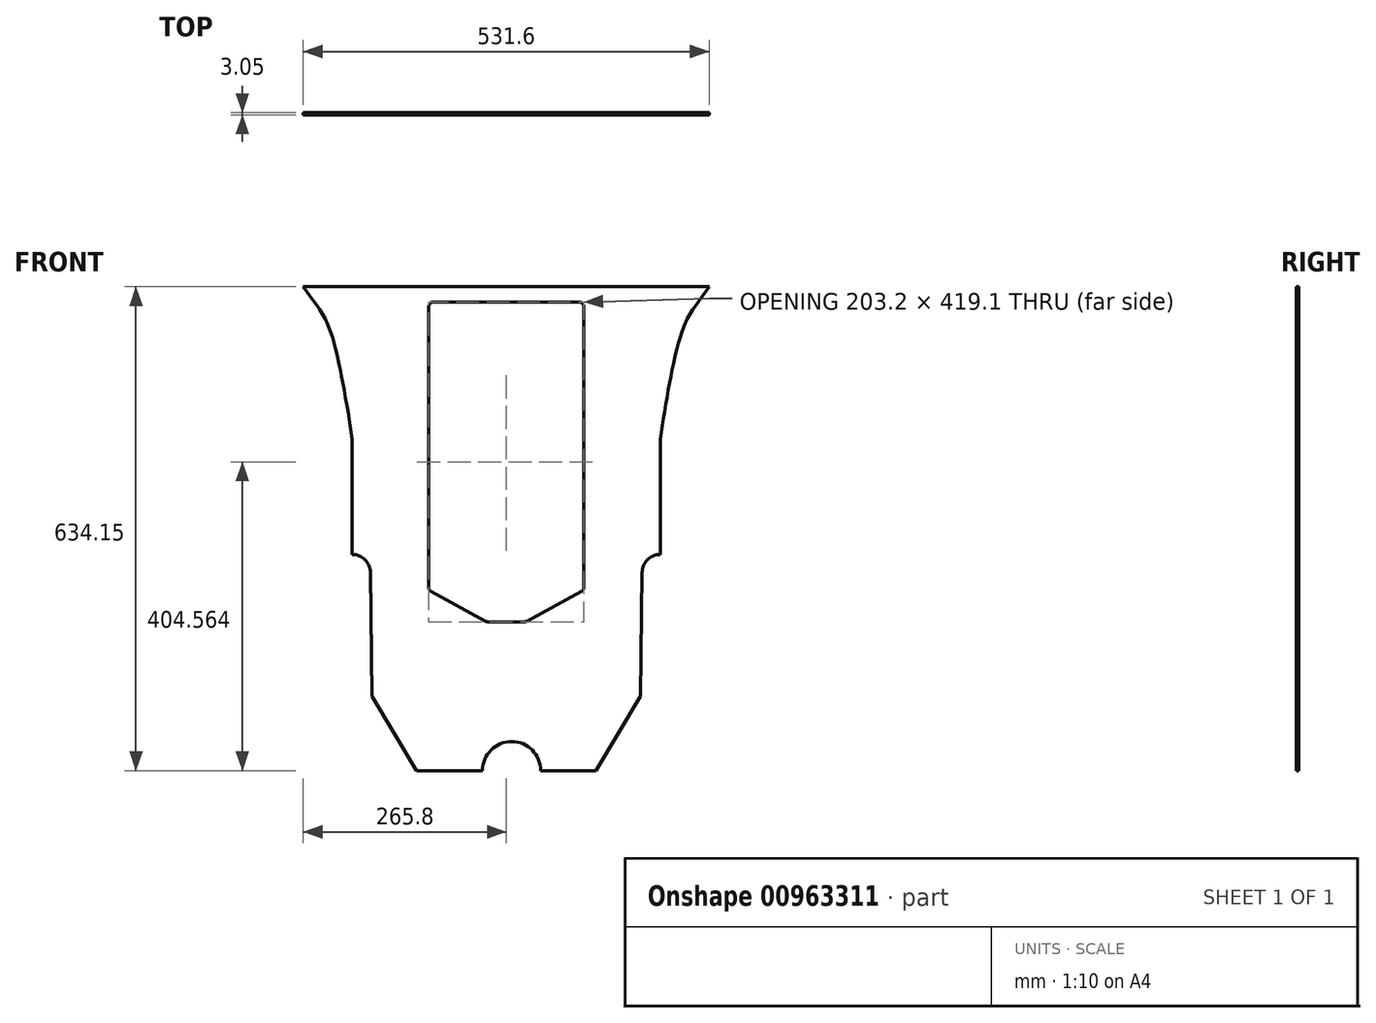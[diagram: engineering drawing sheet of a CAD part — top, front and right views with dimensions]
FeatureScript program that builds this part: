
annotation { "Feature Type Name" : "Feature", "Feature Type Description" : "" }
export const myFeature = defineFeature(function(context is Context, id is Id, definition is map)
    precondition{}
    {
        {
            var Q0;
            Q0=qCreatedBy(makeId("Front.planeOp"),FACE);
            var sketch = newSketch(context, id + "F0", { "sketchPlane" : qUnion([Q0])});
            skPoint(sketch, "E0.orphan", {"position": v(0, 374.32) * mm});
            skLineSegment(sketch, "E1", {"start": v(-101.6, 219.87) * mm, "end": v(-101.6, -147.74) * mm});
            skLineSegment(sketch, "E2", {"start": v(-95.25, 226.22) * mm, "end": v(95.25, 226.22) * mm});
            skLineSegment(sketch, "E3", {"start": v(23.35, -192.88) * mm, "end": v(-23.35, -192.88) * mm});
            skLineSegment(sketch, "E4", {"start": v(-98.26, -153.33) * mm, "end": v(-26.37, -192.11) * mm});
            skLineSegment(sketch, "E5", {"start": v(0, 268.15) * mm, "end": v(0, -423.16) * mm, "construction": true});
            skPoint(sketch, "E5.startSnap0", {"position": v(0, 226.22) * mm});
            skLineSegment(sketch, "E6.MirrorCS", {"start": v(98.26, -153.33) * mm, "end": v(26.37, -192.11) * mm});
            skPoint(sketch, "E7.orphan", {"position": v(-101.6, -192.88) * mm});
            skPoint(sketch, "E8.end.orphan", {"position": v(101.6, -192.88) * mm});
            skLineSegment(sketch, "E9", {"start": v(0, 246.26) * mm, "end": v(-228.6, 246.26) * mm});
            skLineSegment(sketch, "E10.MirrorCS", {"start": v(0, 246.26) * mm, "end": v(228.6, 246.26) * mm});
            skLineSegment(sketch, "E11", {"start": v(-117.35, -387.89) * mm, "end": v(-31.03, -387.89) * mm});
            skLineSegment(sketch, "E12.MirrorCS", {"start": v(117.35, -387.89) * mm, "end": v(45.17, -387.89) * mm});
            skLineSegment(sketch, "E13", {"start": v(-117.35, -387.89) * mm, "end": v(-175.81, -289.99) * mm});
            skLineSegment(sketch, "E14.MirrorCS", {"start": v(117.35, -387.89) * mm, "end": v(175.81, -289.99) * mm});
            skArc(sketch, "E15", {"start": v(-177.97, -128.4) * mm, "mid": v(-184.97, -111.51) * mm, "end": v(-201.85, -104.52) * mm});
            skArc(sketch, "E16.MirrorC", {"start": v(177.97, -128.4) * mm, "mid": v(184.97, -111.51) * mm, "end": v(201.85, -104.52) * mm});
            skLineSegment(sketch, "E17", {"start": v(-201.85, -198.24) * mm, "end": v(-201.85, -198.93) * mm});
            skLineSegment(sketch, "E18", {"start": v(201.85, -198.24) * mm, "end": v(201.85, -198.93) * mm});
            skLineSegment(sketch, "E19", {"start": v(101.6, 219.87) * mm, "end": v(101.6, -147.74) * mm});
            skFitSpline(sketch, "E20", {"points": [v(-201.85, 46.36) * mm, v(-209.18, 93.5) * mm, v(-217.88, 139.91) * mm, v(-223.69, 166.02) * mm, v(-236.74, 203.01) * mm, v(-252.7, 227.67) * mm], "startDerivative": vector(-30, 204.66) * mm, "endDerivative": vector(-94.57, 126.16) * mm});
            skFitSpline(sketch, "E21.MirrorCS", {"points": [v(201.85, 46.36) * mm, v(209.18, 93.5) * mm, v(217.88, 139.91) * mm, v(223.69, 166.02) * mm, v(236.74, 203.01) * mm, v(252.7, 227.67) * mm], "startDerivative": vector(30, 204.66) * mm, "endDerivative": vector(94.57, 126.16) * mm});
            skPoint(sketch, "E22.orphan", {"position": v(-201.85, 246.26) * mm});
            skPoint(sketch, "E23.orphan", {"position": v(201.85, 246.26) * mm});
            skLineSegment(sketch, "E24.trimOffspring", {"start": v(201.85, -104.52) * mm, "end": v(201.85, 46.36) * mm});
            skLineSegment(sketch, "E25", {"start": v(-201.85, -246.4) * mm, "end": v(-201.86, -246.38) * mm});
            skLineSegment(sketch, "E26", {"start": v(201.85, -246.4) * mm, "end": v(201.9, -246.38) * mm});
            skArc(sketch, "E27", {"start": v(45.17, -387.89) * mm, "mid": v(7.07, -349.79) * mm, "end": v(-31.03, -387.89) * mm});
            skPoint(sketch, "E28.orphan", {"position": v(0, -387.89) * mm});
            skLineSegment(sketch, "E29.trimOffspring", {"start": v(-201.85, -104.52) * mm, "end": v(-201.85, 46.36) * mm});
            skPoint(sketch, "E30.visualSharp", {"position": v(-101.6, 226.22) * mm});
            skArc(sketch, "E30.filletArc", {"start": v(-95.25, 226.22) * mm, "mid": v(-99.74, 224.36) * mm, "end": v(-101.6, 219.87) * mm});
            skPoint(sketch, "E31.visualSharp", {"position": v(101.6, 226.22) * mm});
            skArc(sketch, "E31.filletArc", {"start": v(101.6, 219.87) * mm, "mid": v(99.74, 224.36) * mm, "end": v(95.25, 226.22) * mm});
            skPoint(sketch, "E32.visualSharp", {"position": v(-101.6, -151.53) * mm});
            skArc(sketch, "E32.filletArc", {"start": v(-101.6, -147.74) * mm, "mid": v(-100.7, -151) * mm, "end": v(-98.26, -153.33) * mm});
            skPoint(sketch, "E33.visualSharp", {"position": v(-24.96, -192.88) * mm});
            skArc(sketch, "E33.filletArc", {"start": v(-26.37, -192.11) * mm, "mid": v(-24.9, -192.68) * mm, "end": v(-23.35, -192.88) * mm});
            skPoint(sketch, "E34.visualSharp", {"position": v(24.96, -192.88) * mm});
            skArc(sketch, "E34.filletArc", {"start": v(23.35, -192.88) * mm, "mid": v(24.9, -192.68) * mm, "end": v(26.37, -192.11) * mm});
            skPoint(sketch, "E35.visualSharp", {"position": v(101.6, -151.53) * mm});
            skArc(sketch, "E35.filletArc", {"start": v(98.26, -153.33) * mm, "mid": v(100.7, -151) * mm, "end": v(101.6, -147.74) * mm});
            skLineSegment(sketch, "E36", {"start": v(-252.7, 227.67) * mm, "end": v(-265.8, 246.26) * mm});
            skLineSegment(sketch, "E37", {"start": v(-265.8, 246.26) * mm, "end": v(-228.6, 246.26) * mm});
            skLineSegment(sketch, "E38.MirrorCS", {"start": v(252.7, 227.67) * mm, "end": v(265.8, 246.26) * mm});
            skLineSegment(sketch, "E39.MirrorCS", {"start": v(265.8, 246.26) * mm, "end": v(228.6, 246.26) * mm});
            skPoint(sketch, "E40.MirrorCS.end.orphan", {"position": v(228.6, 246.26) * mm});
            skLineSegment(sketch, "E41", {"start": v(-177.97, -128.4) * mm, "end": v(-175.81, -289.99) * mm});
            skLineSegment(sketch, "E42.MirrorCS", {"start": v(177.97, -128.4) * mm, "end": v(175.81, -289.99) * mm});
            skPoint(sketch, "E43.center.orphan", {"position": v(-201.85, -222.65) * mm});
            skSolve(sketch);
        }
        {
            var Q0;
            Q0=qSketchRegion(id+"F0",true);
            extrude(context, id + "F1", {"entities" : qUnion([Q0]), "depth" : 3.05 * mm, "offsetDistance" : 25.4 * mm});
        }
    });
